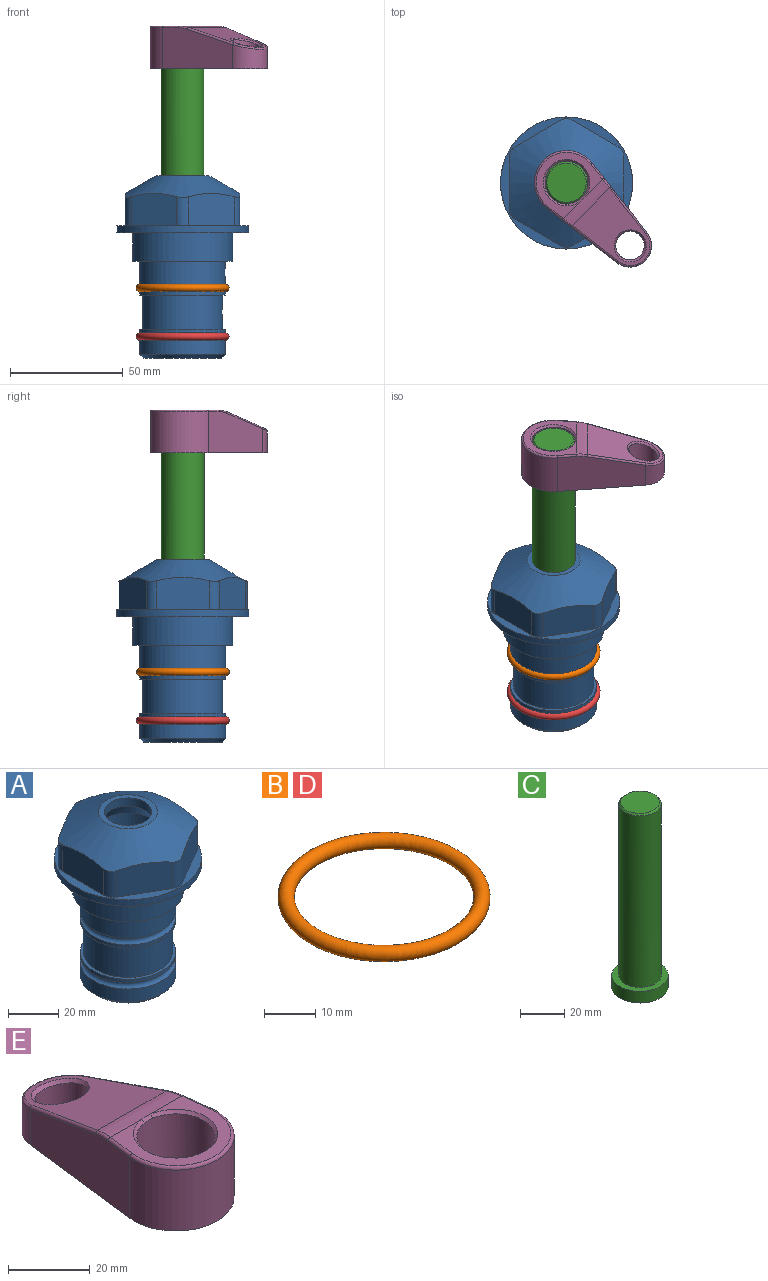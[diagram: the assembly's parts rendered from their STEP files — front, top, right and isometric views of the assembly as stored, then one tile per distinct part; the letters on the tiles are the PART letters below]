
ASSEMBLY  parts=5 mates=4
PART A: 36 faces, bbox 58.7x58.7x81 mm
  f0: cylinder r=17.78mm len=35.56mm, axis (0,0,1), area 1670.8mm2, adj f23,f24,f31
  f1: cylinder r=19.05mm len=38.1mm, axis (0,0,1), area 1191.9mm2, adj f26,f27,f30
  f2: plane 58.66x58.66mm, normal (0,0,-1), area 1150.6mm2, adj f3,f28
  f3: cylinder r=29.33mm len=58.66mm, axis (0,0,-1), area 585.1mm2, adj f2,f4
  f4: plane 58.66x58.66mm, normal (0,0,1), area 475.9mm2, adj f3,f5,f6,f7,f8,f9,f10,f11
  f5: plane 20.32x14.34mm, normal (-0.5,0.87,0), area 324.4mm2, adj f4,f15,f16,f17
  f6: plane 20.32x14.34mm, normal (0.5,0.87,0), area 324.4mm2, adj f4,f14,f15,f17
  f7: plane 23.48x14.34mm, normal (1,0,0), area 324.4mm2, adj f4,f13,f14,f17
  f8: plane 20.32x14.34mm, normal (0.5,-0.87,0), area 324.4mm2, adj f4,f12,f13,f17
  f9: plane 20.32x14.34mm, normal (-0.5,-0.87,0), area 324.4mm2, adj f4,f11,f12,f17
  f10: plane 23.48x14.34mm, normal (-1,0,0), area 324.4mm2, adj f4,f11,f16,f17
  f11: cylinder r=5.08mm len=12.85mm, axis (0,0,-1), area 67.2mm2, adj f4,f9,f10,f17
  f12: cylinder r=5.08mm len=12.85mm, axis (0,0,-1), area 67.2mm2, adj f4,f8,f9,f17
  f13: cylinder r=5.08mm len=12.85mm, axis (0,0,-1), area 67.2mm2, adj f4,f7,f8,f17
  f14: cylinder r=5.08mm len=12.85mm, axis (0,0,-1), area 67.2mm2, adj f4,f6,f7,f17
  f15: cylinder r=5.08mm len=12.85mm, axis (0,0,-1), area 67.2mm2, adj f4,f5,f6,f17
  f16: cylinder r=5.08mm len=12.85mm, axis (0,0,-1), area 67.2mm2, adj f4,f5,f10,f17
  f17: cone r=11.73mm half-angle=60deg, axis (0,0,-1), area 2071.8mm2, adj f5,f6,f7,f8,f9,f10,f11,f12
  f18: plane 23.46x23.46mm, normal (0,0,1), area 147.4mm2, adj f17,f35
  f19: plane 34.93x34.93mm, normal (0,0,-1), area 958mm2, adj f29
  f20: cylinder r=19.05mm len=38.1mm, axis (0,0,1), area 760.1mm2, adj f21,f29
  f21: torus R=19.05mm, axis (0,0,1), area 565.3mm2, adj f20,f22
  f22: cylinder r=19.05mm len=38.1mm, axis (0,0,1), area 190mm2, adj f21,f23
  f23: plane 38.1x38.1mm, normal (0,0,1), area 146.9mm2, adj f0,f22
  f24: plane 38.1x38.1mm, normal (0,0,-1), area 146.9mm2, adj f0,f25
  f25: cylinder r=19.05mm len=38.1mm, axis (0,0,1), area 190mm2, adj f24,f26
  f26: torus R=19.05mm, axis (0,0,1), area 565.3mm2, adj f1,f25
  f27: plane 44.45x44.45mm, normal (0,0,-1), area 411.7mm2, adj f1,f28
  f28: cylinder r=22.23mm len=44.45mm, axis (0,0,1), area 1773.5mm2, adj f2,f27
  f29: cone r=19.05mm half-angle=45deg, axis (0,0,1), area 257.5mm2, adj f19,f20
  f30: cylinder r=3.17mm len=6.75mm, axis (-1,0,0), area 128mm2, adj f1,f33
  f31: cylinder r=3.17mm len=6.35mm, axis (-1,0,0), area 102.5mm2, adj f0,f33
  f32: plane 25.4x25.4mm, normal (0,0,1), area 506.7mm2, adj f33
  f33: cylinder r=12.7mm len=66.42mm, axis (0,0,-1), area 5236.2mm2, adj f30,f31,f32,f34
  f34: cone r=9.53mm half-angle=30deg, axis (0,0,-1), area 443.4mm2, adj f33,f35
  f35: cylinder r=9.53mm len=19.05mm, axis (0,0,-1), area 240.9mm2, adj f18,f34
PART B: 1 faces, bbox 44.7x44.7x3.2 mm
  f0: torus R=19.05mm, axis (0,0,1), area 1193.9mm2
PART C: 6 faces, bbox 25.4x25.4x101.6 mm
  f0: plane 17.46x17.46mm, normal (0,0,1), area 239.5mm2, adj f5
  f1: plane 25.4x25.4mm, normal (0,0,-1), area 506.7mm2, adj f2
  f2: cylinder r=12.7mm len=25.4mm, axis (0,0,1), area 506.7mm2, adj f1,f3
  f3: plane 25.4x25.4mm, normal (0,0,1), area 221.7mm2, adj f2,f4
  f4: cylinder r=9.53mm len=94.46mm, axis (0,0,1), area 5653mm2, adj f3,f5
  f5: cone r=8.73mm half-angle=45deg, axis (0,0,-1), area 64.4mm2, adj f0,f4
PART D: same geometry as B
PART E: 31 faces, bbox 31.7x65.5x19.8 mm
  f0: plane 39.12x18.26mm, normal (0.99,0.12,0), area 612.2mm2, adj f1,f4,f7,f11,f13,f15
  f1: cylinder r=9.53mm len=18.91mm, axis (0,0,-1), area 296.1mm2, adj f0,f2,f7,f17
  f2: plane 39.12x18.26mm, normal (-0.99,0.12,0), area 612.2mm2, adj f1,f4,f7,f12,f14,f16
  f3: cylinder r=6.35mm len=12.7mm, axis (0,0,-1), area 362.4mm2, adj f7,f18
  f4: cylinder r=14.29mm len=28.58mm, axis (0,0,-1), area 882.2mm2, adj f0,f2,f7,f10
  f5: cylinder r=9.53mm len=19.05mm, axis (0,0,-1), area 1092.6mm2, adj f7,f19,f20
  f6: plane 26.99x23.69mm, normal (0,0,1), area 216.2mm2, adj f9,f10,f11,f12,f19
  f7: plane 63.5x28.58mm, normal (0,0,-1), area 661.8mm2, adj f0,f1,f2,f3,f4,f5,f22,f23
  f8: plane 33.52x23.6mm, normal (0,0.26,0.97), area 486mm2, adj f9,f15,f16,f17,f18
  f9: cylinder r=19.05mm len=24.72mm, axis (1,0,0), area 120.4mm2, adj f6,f8,f13,f14,f20
  f10: torus R=13.49mm, axis (0,0,1), area 59mm2, adj f4,f6,f11,f12
  f11: cylinder r=0.79mm len=8.67mm, axis (0.12,-0.99,0), area 10.8mm2, adj f0,f6,f10,f13
  f12: cylinder r=0.79mm len=8.67mm, axis (0.12,0.99,0), area 10.8mm2, adj f2,f6,f10,f14
  f13: bspline ~4.95x1.42mm, area 6.1mm2, adj f0,f9,f11,f15
  f14: bspline ~4.95x1.42mm, area 6.1mm2, adj f2,f9,f12,f16
  f15: cylinder r=0.79mm len=25.95mm, axis (0.12,-0.96,0.26), area 32.9mm2, adj f0,f8,f13,f17
  f16: cylinder r=0.79mm len=25.95mm, axis (0.12,0.96,-0.26), area 32.9mm2, adj f2,f8,f14,f17
  f17: bspline ~18.91x8.38mm, area 30mm2, adj f1,f8,f15,f16
  f18: bspline ~14.29x14.29mm, area 48.3mm2, adj f3,f8
  f19: cone r=9.53mm half-angle=45deg, axis (0,0,1), area 66.5mm2, adj f5,f6,f20
  f20: bspline ~3.22x0.96mm, area 3.5mm2, adj f5,f9,f19
  f21: plane 2.75x2.72mm, normal (0,0,-1), area 2.9mm2, adj f23,f25,f28
  f22: plane 23.05x15.88mm, normal (-0.99,-0.12,0), area 323.6mm2, adj f7,f25,f26,f27,f28,f29
  f23: plane 23.05x15.88mm, normal (0.99,-0.12,0), area 323.6mm2, adj f7,f21,f25,f27,f28,f30
  f24: cylinder r=9.53mm len=10.69mm, axis (0,0,-1), area 114.7mm2, adj f7,f27,f29,f30
  f25: cylinder r=12.7mm len=20.59mm, axis (0,0,-1), area 381.1mm2, adj f7,f21,f22,f23,f26,f28
  f26: plane 2.75x2.72mm, normal (0,0,-1), area 2.9mm2, adj f22,f25,f28
  f27: plane 19.72x18.37mm, normal (0,-0.26,-0.97), area 291.8mm2, adj f22,f23,f24,f28,f29,f30
  f28: cylinder r=15.88mm len=19.92mm, axis (1,0,0), area 54.8mm2, adj f21,f22,f23,f25,f26,f27
  f29: cylinder r=1.59mm len=11mm, axis (0,0,-1), area 34.7mm2, adj f7,f22,f24,f27
  f30: cylinder r=1.59mm len=11mm, axis (0,0,-1), area 34.7mm2, adj f7,f23,f24,f27
PLACE A at identity fixed
PLACE B at identity
PLACE C rot(axis=(0,0,-1),134.7deg) t=(0,0,27.55)mm
PLACE D t=(0,0,-21.59)mm
PLACE E rot(axis=(0,0,-1),134.7deg) t=(0,0,28.35)mm
MATE cylindrical A.f0 <-> C.f2  axis (0,0,1) through (0,0,-50.55)mm
MATE fastened E.f4 <-> C.f2  axis (0,0,-1) through (0,0,91.05)mm
MATE fastened B.f0 <-> A.f0  axis (0,0,1) through (0,0,-24.51)mm
MATE fastened D.f0 <-> A.f0  axis (0,0,1) through (0,0,-46.1)mm
